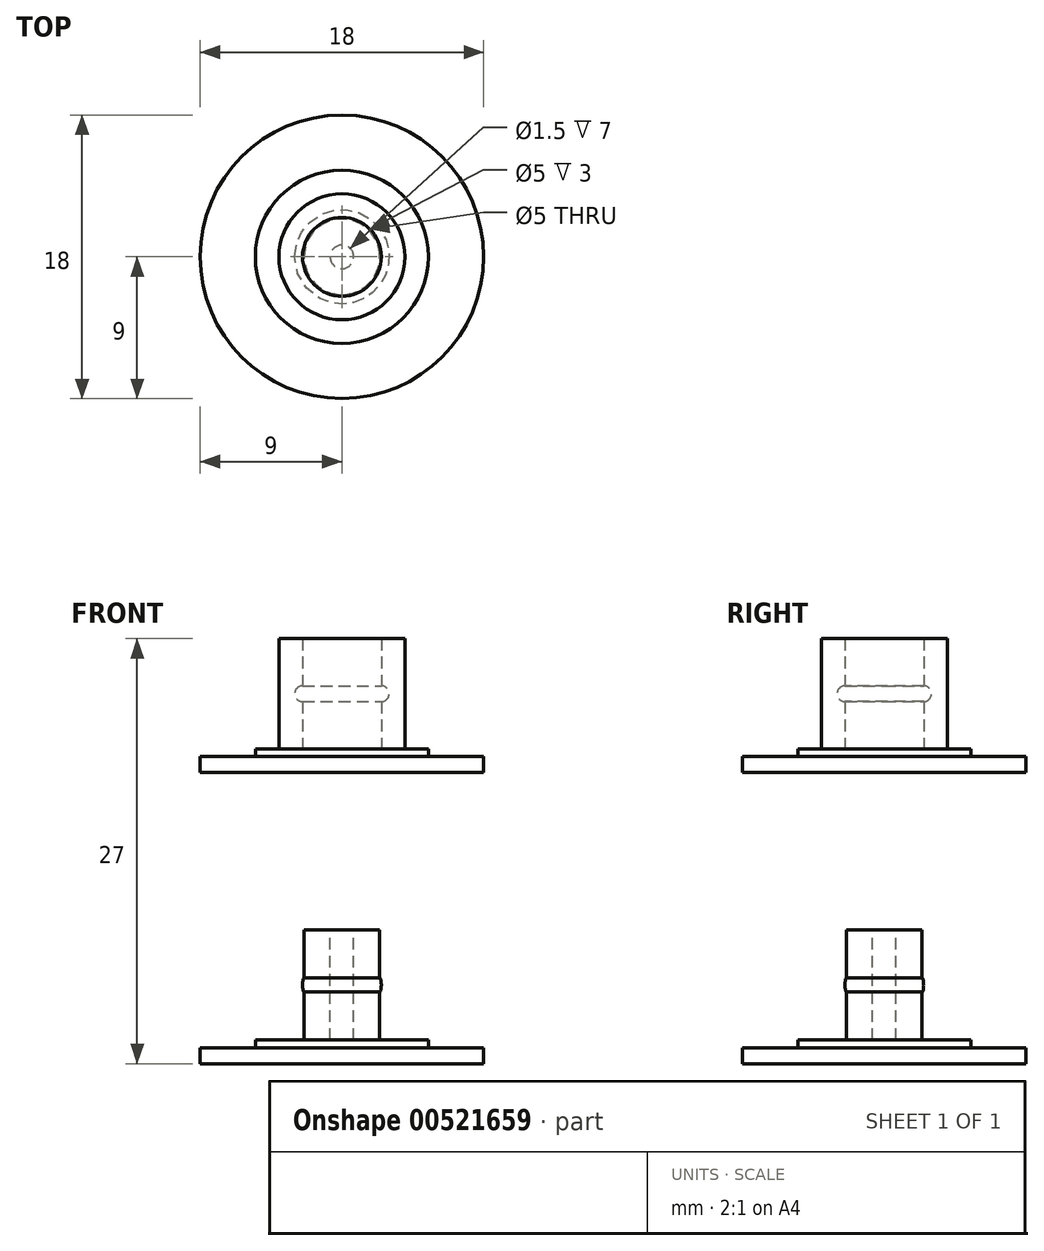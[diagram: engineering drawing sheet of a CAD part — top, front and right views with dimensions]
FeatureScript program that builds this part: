
annotation { "Feature Type Name" : "Feature", "Feature Type Description" : "" }
export const myFeature = defineFeature(function(context is Context, id is Id, definition is map)
    precondition{}
    {
        {
            var Q0;
            Q0=qCreatedBy(makeId("Front.planeOp"),FACE);
            var sketch = newSketch(context, id + "F0", { "sketchPlane" : qUnion([Q0])});
            skLineSegment(sketch, "E0", {"start": v(0, 0) * mm, "end": v(-9, 0) * mm});
            skLineSegment(sketch, "E1", {"start": v(-9, 0) * mm, "end": v(-9, 1) * mm});
            skLineSegment(sketch, "E2", {"start": v(-9, 1) * mm, "end": v(-5.5, 1) * mm});
            skLineSegment(sketch, "E3", {"start": v(-5.5, 1) * mm, "end": v(-5.5, 1.5) * mm});
            skLineSegment(sketch, "E4", {"start": v(-4, 1.5) * mm, "end": v(-5.5, 1.5) * mm});
            skLineSegment(sketch, "E5", {"start": v(-4, 1.5) * mm, "end": v(-4, 8.5) * mm});
            skLineSegment(sketch, "E6", {"start": v(-4, 8.5) * mm, "end": v(-2.5, 8.5) * mm});
            skLineSegment(sketch, "E7", {"start": v(0, -18.5) * mm, "end": v(-9, -18.5) * mm});
            skLineSegment(sketch, "E8", {"start": v(-9, -18.5) * mm, "end": v(-9, -17.5) * mm});
            skLineSegment(sketch, "E9", {"start": v(-9, -17.5) * mm, "end": v(-5.5, -17.5) * mm});
            skLineSegment(sketch, "E10", {"start": v(-5.5, -17.5) * mm, "end": v(-5.5, -17) * mm});
            skLineSegment(sketch, "E11", {"start": v(-2.5, 1.5) * mm, "end": v(0, 1.5) * mm});
            skLineSegment(sketch, "E12", {"start": v(0, 0) * mm, "end": v(0, 1.5) * mm});
            skLineSegment(sketch, "E13", {"start": v(0, -17) * mm, "end": v(-0.75, -17) * mm});
            skLineSegment(sketch, "E14", {"start": v(-0.75, -17) * mm, "end": v(-0.75, -10) * mm});
            skLineSegment(sketch, "E15", {"start": v(0, -17) * mm, "end": v(0, -18.5) * mm});
            skLineSegment(sketch, "E16", {"start": v(-2.5, 8.5) * mm, "end": v(-2.5, 5.5) * mm});
            skLineSegment(sketch, "E17", {"start": v(-2.4, -17) * mm, "end": v(-2.4, -13.95) * mm});
            skLineSegment(sketch, "E18", {"start": v(-2.4, -10) * mm, "end": v(-0.75, -10) * mm});
            skLineSegment(sketch, "E19", {"start": v(-5.5, -17) * mm, "end": v(-2.4, -17) * mm});
            skPoint(sketch, "E20", {"position": v(-2.5, 5) * mm});
            skPoint(sketch, "E21", {"position": v(-2.4, -13.5) * mm});
            skArc(sketch, "E22", {"start": v(-2.5, 5.5) * mm, "mid": v(-3, 5) * mm, "end": v(-2.5, 4.5) * mm});
            skLineSegment(sketch, "E23.trimOffspring", {"start": v(-2.5, 4.5) * mm, "end": v(-2.5, 1.5) * mm});
            skEllipticalArc(sketch, "E24", {});
            skPoint(sketch, "E25", {"position": v(-2.4, -13.05) * mm});
            skLineSegment(sketch, "E26.trimOffspring", {"start": v(-2.4, -13.05) * mm, "end": v(-2.4, -10) * mm});
            const initialGuessF0  = {"E24": [-0.0024, -0.0135, 0, -1, 0.00045, 0.0001, 3.1415926535897927, 6.283185307179585]};
            skSetInitialGuess(sketch, initialGuessF0);
            skSolve(sketch);
        }
        {
            var Q0;
            Q0=makeQuery(id+"F0.imprint","IMPRINT",FACE,{"disambiguationData":[TD([[makeQuery(id+"F0.imprint","IMPRINT",EDGE,{"derivedFrom":sQuery(id+"F0.wireOp",EDGE,"E0")}),-1.0]])]});
            var Q1;
            Q1=sQuery(id+"F0.wireOp",EDGE,"E12");
            revolve(context, id + "F1", {"entities" : qUnion([Q0]), "axis" : qUnion([Q1]), "revolveType" : RevolveType.ONE_DIRECTION, "angle" : 360 * degree});
        }
        {
            var Q0;
            Q0=makeQuery(id+"F0.imprint","IMPRINT",FACE,{"disambiguationData":[TD([[makeQuery(id+"F0.imprint","IMPRINT",EDGE,{"derivedFrom":sQuery(id+"F0.wireOp",EDGE,"E7")}),-1.0]])]});
            var Q1;
            Q1=sQuery(id+"F0.wireOp",EDGE,"E15");
            revolve(context, id + "F2", {"entities" : qUnion([Q0]), "axis" : qUnion([Q1]), "revolveType" : RevolveType.FULL});
        }
    });
